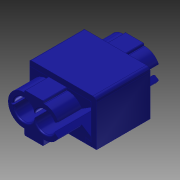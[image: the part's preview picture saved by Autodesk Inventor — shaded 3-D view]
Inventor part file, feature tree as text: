
AUTODESK INVENTOR PART (.ipt)
format: ipt  version: 2014 (Build 180170000, 170)  size: 420,352 bytes
history: native  units: in
note: dims shown in document units (in); Inventor stores cm internally (conversion verified against a paired STEP export)
features: extrude x9, sketch x8, projected_geometry x8, fillet x7, chamfer x1
ambient origin geometry x8: Origin, YZ Plane, XZ Plane, XY Plane, X Axis, Y Axis, Z Axis, Center Point
bodies: Solid1 (feature_tree), Solid2 (feature_tree)
feature tree (33):
  sketch  "Sketch2"  dims[d3=0.3in d4=0.47in]
  extrude  "Extrusion1"  Depth=0.47in
  extrude  "Extrusion2"  Depth=0.238in
  extrude  "Extrusion3"  Depth=0.145in
  extrude  "Extrusion4"  Depth=0.16in
  extrude  "Extrusion5"  Depth=0.771in TaperAngle=0.0deg
  extrude  "Extrusion6"  Depth=0.771in
  fillet  "Fillet1"  Radius=0.0425in
  extrude  "Extrusion7"  Depth=0.771in TaperAngle=0.0deg
  extrude  "Extrusion8"  Depth=0.005in
  extrude  "Extrusion9"  Depth=0.005in
  chamfer  "Chamfer1"  Distance=0.332in
  fillet  "Fillet2"  Radius=0.057in
  fillet  "Fillet3"  Radius=0.01in
  fillet  "Fillet4"  Radius=0.01in
  fillet  "Fillet5"  Radius=0.01in
  fillet  "Fillet6"  Radius=0.01in
  fillet  "Fillet7"  Radius=0.0435in
  sketch  "Sketch3"  dims[d5=0.238in d6=0.238in]
  projected_geometry  "Projected Loop1"
  sketch  "Sketch4"  dims[d7=0.145in d9=0.0135in]
  projected_geometry  "Projected Loop2"
  sketch  "Sketch5"  dims[d10=0.16in d11=0.16in]
  projected_geometry  "Projected Loop3"
  sketch  "Sketch6"  dims[d12=0.4125in d13=0.0in d14=0.771in d15=0.0in]
  projected_geometry  "Projected Loop4"
  sketch  "Sketch7"  dims[d16=0.771in d17=0.0in d18=0.0425in d19=0.0425in]
  projected_geometry  "Projected Loop5"
  sketch  "Sketch8"  dims[d20=0.771in d21=0.0in d22=0.02in d23=0.0in]
  sketch  "Sketch9"  dims[d24=0.0745in d25=0.118in d26=0.118in d27=0.332in d28=0.057in d29=0.057in d30=0.01in d31=0.0in d32=0.01in d33=0.01in d34=0.0in d35=0.01in d36=0.0in d37=0.0435in d38=0.0435in d39=0.01in d40=0.0in d41=0.002in d42=0.125in d43=45.0deg d44=0.01in d45=0.03in d46=0.01in d47=0.01in d48=0.01in d49=0.005in]
  projected_geometry  "Projected Loop6"
  projected_geometry  "Projected Loop7"
  projected_geometry  "Projected Loop8"
